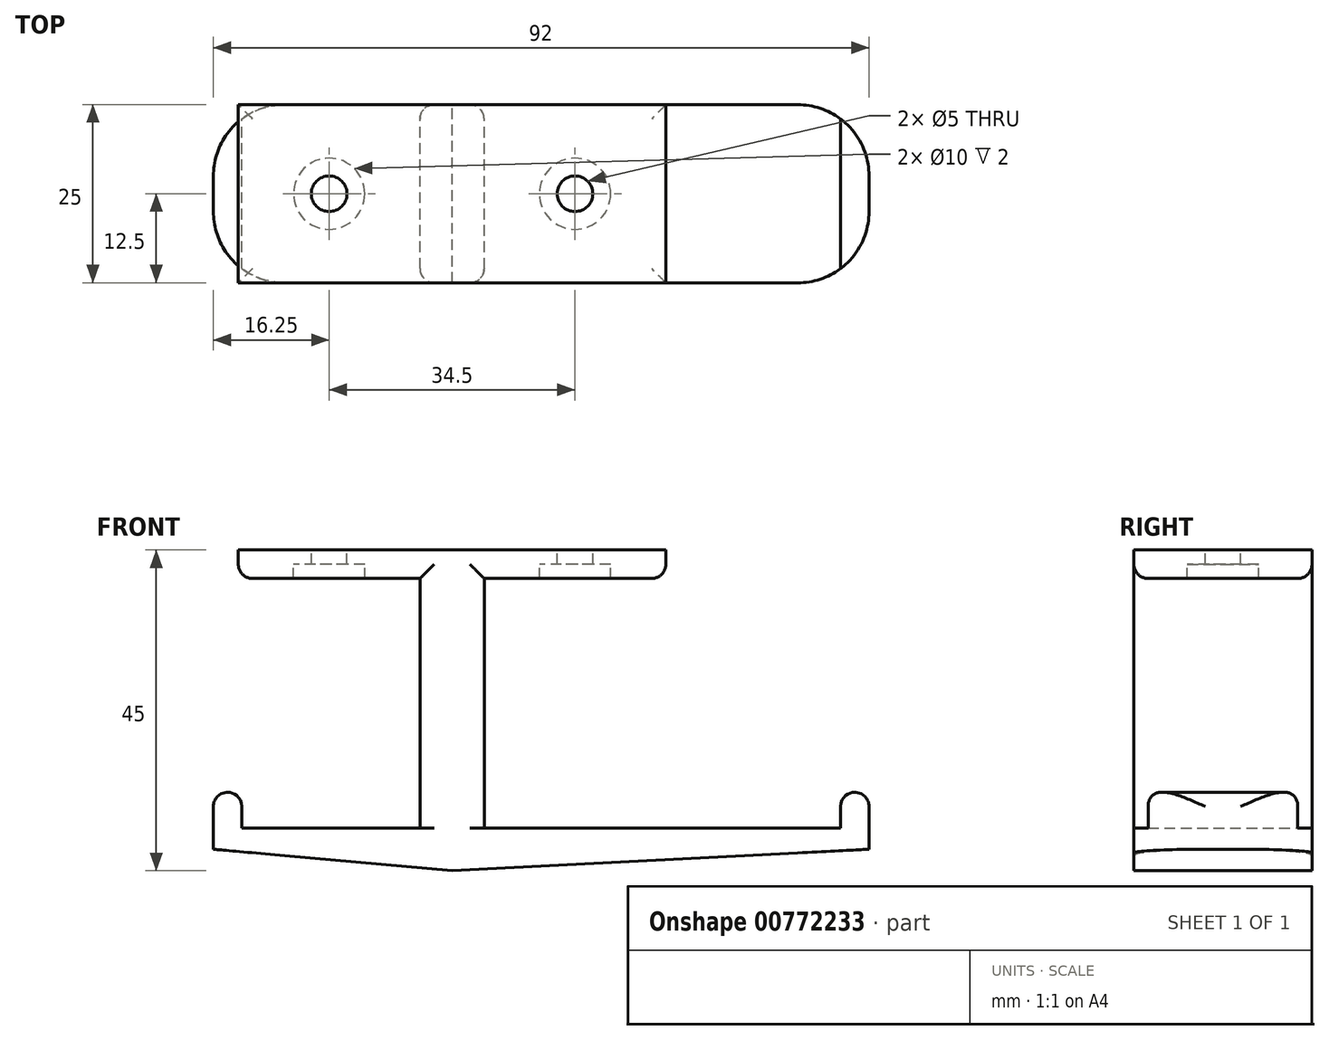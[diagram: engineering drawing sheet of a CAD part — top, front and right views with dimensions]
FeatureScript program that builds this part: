
annotation { "Feature Type Name" : "Feature", "Feature Type Description" : "" }
export const myFeature = defineFeature(function(context is Context, id is Id, definition is map)
    precondition{}
    {
        {
            var Q0;
            Q0=qCreatedBy(makeId("Front.planeOp"),FACE);
            var sketch = newSketch(context, id + "F0", { "sketchPlane" : qUnion([Q0])});
            skLineSegment(sketch, "E0", {"start": v(54.5, -39) * mm, "end": v(4.5, -39) * mm});
            skLineSegment(sketch, "E1", {"start": v(4.5, -39) * mm, "end": v(4.5, -4) * mm});
            skLineSegment(sketch, "E2", {"start": v(4.5, -4) * mm, "end": v(30, -4) * mm});
            skLineSegment(sketch, "E3", {"start": v(30, -4) * mm, "end": v(30, 0) * mm});
            skLineSegment(sketch, "E4", {"start": v(30, 0) * mm, "end": v(-30, 0) * mm});
            skLineSegment(sketch, "E5", {"start": v(-30, -4) * mm, "end": v(-4.5, -4) * mm});
            skLineSegment(sketch, "E6", {"start": v(-4.5, -4) * mm, "end": v(-4.5, -39) * mm});
            skLineSegment(sketch, "E7", {"start": v(-4.5, -39) * mm, "end": v(-29.5, -39) * mm});
            skLineSegment(sketch, "E8", {"start": v(54.5, -39) * mm, "end": v(54.5, -34) * mm});
            skLineSegment(sketch, "E9", {"start": v(54.5, -34) * mm, "end": v(58.5, -34) * mm});
            skLineSegment(sketch, "E10", {"start": v(58.5, -42) * mm, "end": v(0, -45) * mm});
            skLineSegment(sketch, "E11", {"start": v(0, -45) * mm, "end": v(-33.5, -42) * mm});
            skLineSegment(sketch, "E12", {"start": v(-33.5, -42) * mm, "end": v(-33.5, -34) * mm});
            skLineSegment(sketch, "E13", {"start": v(-33.5, -34) * mm, "end": v(-29.5, -34) * mm});
            skLineSegment(sketch, "E14", {"start": v(-29.5, -34) * mm, "end": v(-29.5, -39) * mm});
            skLineSegment(sketch, "E15", {"start": v(58.5, -34) * mm, "end": v(58.5, -42) * mm});
            skLineSegment(sketch, "E16", {"start": v(-30, 0) * mm, "end": v(-30, -4) * mm});
            skLineSegment(sketch, "E17", {"start": v(0, 0) * mm, "end": v(0, -45) * mm, "construction": true});
            skSolve(sketch);
        }
        {
            var Q0;
            Q0=makeQuery(id+"F0.imprint","IMPRINT",FACE,{"disambiguationData":[TD([[makeQuery(id+"F0.imprint","IMPRINT",EDGE,{"derivedFrom":sQuery(id+"F0.wireOp",EDGE,"E0")}),1.0]])]});
            extrude(context, id + "F1", {"entities" : qUnion([Q0]), "depth" : 25 * mm, "offsetDistance" : 25 * mm, "symmetric" : true});
        }
        {
            var Q0;
            Q0=makeQuery(id+"F1.opExtrude","SWEPT_FACE",FACE,{"disambiguationData":[OSD([sQuery(id+"F0.wireOp",EDGE,"E2")])]});
            var sketch = newSketch(context, id + "F2", { "sketchPlane" : qUnion([Q0])});
            skLineSegment(sketch, "E18.0", {"start": v(-4.5, 12.5) * mm, "end": v(-4.5, -12.5) * mm, "construction": true});
            skLineSegment(sketch, "E19.0", {"start": v(4.5, 12.5) * mm, "end": v(4.5, -12.5) * mm, "construction": true});
            skLineSegment(sketch, "E20", {"start": v(30, 0) * mm, "end": v(4.5, 0) * mm, "construction": true});
            skLineSegment(sketch, "E21", {"start": v(-4.5, 0) * mm, "end": v(-30, 0) * mm, "construction": true});
            skPoint(sketch, "E22", {"position": v(17.25, 0) * mm});
            skPoint(sketch, "E23", {"position": v(-17.25, 0) * mm});
            skSolve(sketch);
        }
        {
            var Q0;
            Q0=sQuery(id+"F2.wireOp",VERTEX,"E22");
            var Q1;
            Q1=sQuery(id+"F2.wireOp",VERTEX,"E23");
            var Q2;
            Q2=makeQuery(id+"F1.opExtrude","SWEPT_BODY",BODY,{"disambiguationData":[OSD([sQuery(id+"F0.wireOp",EDGE,"E0"),sQuery(id+"F0.wireOp",EDGE,"E1"),sQuery(id+"F0.wireOp",EDGE,"E2"),sQuery(id+"F0.wireOp",EDGE,"E3"),sQuery(id+"F0.wireOp",EDGE,"E4"),sQuery(id+"F0.wireOp",EDGE,"E5"),sQuery(id+"F0.wireOp",EDGE,"E6"),sQuery(id+"F0.wireOp",EDGE,"E7"),sQuery(id+"F0.wireOp",EDGE,"E8"),sQuery(id+"F0.wireOp",EDGE,"E9"),sQuery(id+"F0.wireOp",EDGE,"E10"),sQuery(id+"F0.wireOp",EDGE,"E11"),sQuery(id+"F0.wireOp",EDGE,"E12"),sQuery(id+"F0.wireOp",EDGE,"E13"),sQuery(id+"F0.wireOp",EDGE,"E14"),sQuery(id+"F0.wireOp",EDGE,"E15"),sQuery(id+"F0.wireOp",EDGE,"E16")])]});
            hole(context, id + "F3", {"style" : HoleStyle.C_BORE, "endStyle" : HoleEndStyle.BLIND, "holeDiameter" : 5 * mm, "cBoreDiameter" : 10 * mm, "cBoreDepth" : 2 * mm, "majorDiameter" : 5 * mm, "holeDepth" : 12 * mm, "isTappedThrough" : true, "tappedDepth" : 12 * mm, "tapClearance" : 3, "locations" : qUnion([Q0, Q1]), "scope" : qUnion([Q2]), "startStyle" : HoleStartStyle.PART});
        }
        {
            var Q0;
            Q0=makeQuery(id+"F1.opExtrude","SWEPT_EDGE",EDGE,{"disambiguationData":[OSD([sQuery(id+"F0.wireOp",EDGE,"E9"),sQuery(id+"F0.wireOp",EDGE,"E15")])]});
            var Q1;
            Q1=makeQuery(id+"F1.opExtrude","SWEPT_EDGE",EDGE,{"disambiguationData":[OSD([sQuery(id+"F0.wireOp",EDGE,"E8"),sQuery(id+"F0.wireOp",EDGE,"E9")])]});
            var Q2;
            Q2=makeQuery(id+"F1.opExtrude","SWEPT_EDGE",EDGE,{"disambiguationData":[OSD([sQuery(id+"F0.wireOp",EDGE,"E13"),sQuery(id+"F0.wireOp",EDGE,"E14")])]});
            var Q3;
            Q3=makeQuery(id+"F1.opExtrude","SWEPT_EDGE",EDGE,{"disambiguationData":[OSD([sQuery(id+"F0.wireOp",EDGE,"E12"),sQuery(id+"F0.wireOp",EDGE,"E13")])]});
            var Q4;
            Q4=makeQuery(id+"F1.opExtrude","SWEPT_EDGE",EDGE,{"disambiguationData":[OSD([sQuery(id+"F0.wireOp",EDGE,"E2"),sQuery(id+"F0.wireOp",EDGE,"E3")])]});
            var Q5;
            Q5=makeQuery(id+"F1.opExtrude","CAP_EDGE",EDGE,{"disambiguationData":[OSD([sQuery(id+"F0.wireOp",EDGE,"E2")])],"isStart":false});
            var Q6;
            Q6=makeQuery(id+"F1.opExtrude","CAP_EDGE",EDGE,{"disambiguationData":[OSD([sQuery(id+"F0.wireOp",EDGE,"E5")])],"isStart":false});
            var Q7;
            Q7=makeQuery(id+"F1.opExtrude","SWEPT_EDGE",EDGE,{"disambiguationData":[OSD([sQuery(id+"F0.wireOp",EDGE,"E5"),sQuery(id+"F0.wireOp",EDGE,"E16")])]});
            var Q8;
            Q8=makeQuery(id+"F1.opExtrude","CAP_EDGE",EDGE,{"disambiguationData":[OSD([sQuery(id+"F0.wireOp",EDGE,"E5")])],"isStart":true});
            var Q9;
            Q9=makeQuery(id+"F1.opExtrude","CAP_EDGE",EDGE,{"disambiguationData":[OSD([sQuery(id+"F0.wireOp",EDGE,"E6")])],"isStart":true});
            var Q10;
            Q10=makeQuery(id+"F1.opExtrude","CAP_EDGE",EDGE,{"disambiguationData":[OSD([sQuery(id+"F0.wireOp",EDGE,"E1")])],"isStart":true});
            var Q11;
            Q11=makeQuery(id+"F1.opExtrude","CAP_EDGE",EDGE,{"disambiguationData":[OSD([sQuery(id+"F0.wireOp",EDGE,"E6")])],"isStart":false});
            var Q12;
            Q12=makeQuery(id+"F1.opExtrude","CAP_EDGE",EDGE,{"disambiguationData":[OSD([sQuery(id+"F0.wireOp",EDGE,"E1")])],"isStart":false});
            var Q13;
            Q13=makeQuery(id+"F1.opExtrude","CAP_EDGE",EDGE,{"disambiguationData":[OSD([sQuery(id+"F0.wireOp",EDGE,"E2")])],"isStart":true});
            fillet(context, id + "F4", {"entities" : qUnion([Q0, Q1, Q2, Q3, Q4, Q5, Q6, Q7, Q8, Q9, Q10, Q11, Q12, Q13]), "radius" : 2 * mm, "tangentPropagation" : true, "allowEdgeOverflow" : false});
        }
        {
            var Q0;
            Q0=makeQuery(id+"F1.opExtrude","CAP_EDGE",EDGE,{"disambiguationData":[OSD([sQuery(id+"F0.wireOp",EDGE,"E15")])],"isStart":true});
            var Q1;
            Q1=makeQuery(id+"F1.opExtrude","CAP_EDGE",EDGE,{"disambiguationData":[OSD([sQuery(id+"F0.wireOp",EDGE,"E15")])],"isStart":false});
            var Q2;
            Q2=makeQuery(id+"F1.opExtrude","CAP_EDGE",EDGE,{"disambiguationData":[OSD([sQuery(id+"F0.wireOp",EDGE,"E12")])],"isStart":true});
            var Q3;
            Q3=makeQuery(id+"F1.opExtrude","CAP_EDGE",EDGE,{"disambiguationData":[OSD([sQuery(id+"F0.wireOp",EDGE,"E12")])],"isStart":false});
            fillet(context, id + "F5", {"entities" : qUnion([Q0, Q1, Q2, Q3]), "radius" : 10 * mm, "tangentPropagation" : true, "allowEdgeOverflow" : false});
        }
    });
